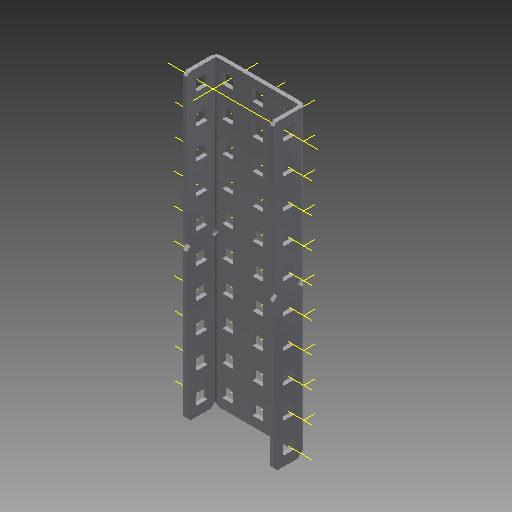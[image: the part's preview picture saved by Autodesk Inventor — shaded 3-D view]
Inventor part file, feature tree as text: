
AUTODESK INVENTOR PART (.ipt)
format: ipt  version: 2017 (Build 210142000, 142)  size: 2,000,896 bytes
history: native  units: in
note: dims shown in document units (in); Inventor stores cm internally (conversion verified against a paired STEP export)
features: other x56, pattern_linear x2, sheet_metal_op x1, extrude x1, imported_body x1, sketch x1
ambient origin geometry x8: Origin, YZ Plane, XZ Plane, XY Plane, X Axis, Y Axis, Z Axis, Center Point
bodies: Body1 (feature_tree)
feature tree (62):
  sheet_metal_op  "Fold1"
  other  "C-Channel"
  extrude  "length cut"  Depth=1.1811in
  other  "Work Point1"
  other  "Work Point2"
  other  "Work Point3"
  other  "top axis"
  other  "front axis"
  other  "back axis"
  pattern_linear  "top axes"  Count1=10  [1 undecoded]
  pattern_linear  "horiz axes"  Spacing1=0.5in  [1 undecoded]
  other  "Left Plane"
  other  "Right Plane"
  imported_body  "Base1"
  sketch  "Sketch1"  dims[d1=0.0in d2=1.1811in d4=0.5in d5=3.937in d7=0.5in d8=3.937in d10=0.5in d12=-5.0in d17=0.0in d18=0.0in d19=0.0in d20=0.0in d21=0.0in]
  other  "Work Axis4"
  other  "Work Axis5"
  other  "Work Axis6"
  other  "Work Axis7"
  other  "Work Axis8"
  other  "Work Axis9"
  other  "Work Axis10"
  other  "Work Axis11"
  other  "Work Axis12"
  other  "Work Axis13"
  other  "Work Axis14"
  other  "Work Axis15"
  other  "Work Axis16"
  other  "Work Axis17"
  other  "Work Axis18"
  other  "Work Axis19"
  other  "Work Axis20"
  other  "Work Axis21"
  other  "Work Axis22"
  other  "Work Axis23"
  other  "Work Axis24"
  other  "Work Axis25"
  other  "Work Axis26"
  other  "Work Axis27"
  other  "Work Axis28"
  other  "Work Axis29"
  other  "Work Axis30"
  other  "Work Axis31"
  other  "Work Axis32"
  other  "Work Axis48"
  other  "Work Axis49"
  other  "Work Axis50"
  other  "Work Axis51"
  other  "Work Axis52"
  other  "Work Axis53"
  other  "Work Axis54"
  other  "Work Axis55"
  other  "Work Axis56"
  other  "Work Axis62"
  other  "Work Axis63"
  other  "Work Axis64"
  other  "Work Axis65"
  other  "Work Axis66"
  other  "Work Axis67"
  other  "Work Axis68"
  other  "Work Axis69"
  other  "Work Axis70"
note: 2 required parameter values undecoded (feature->parameter linkage not recoverable at this tier; creation-order binding heuristic only, values carry confidence <= 0.55)
